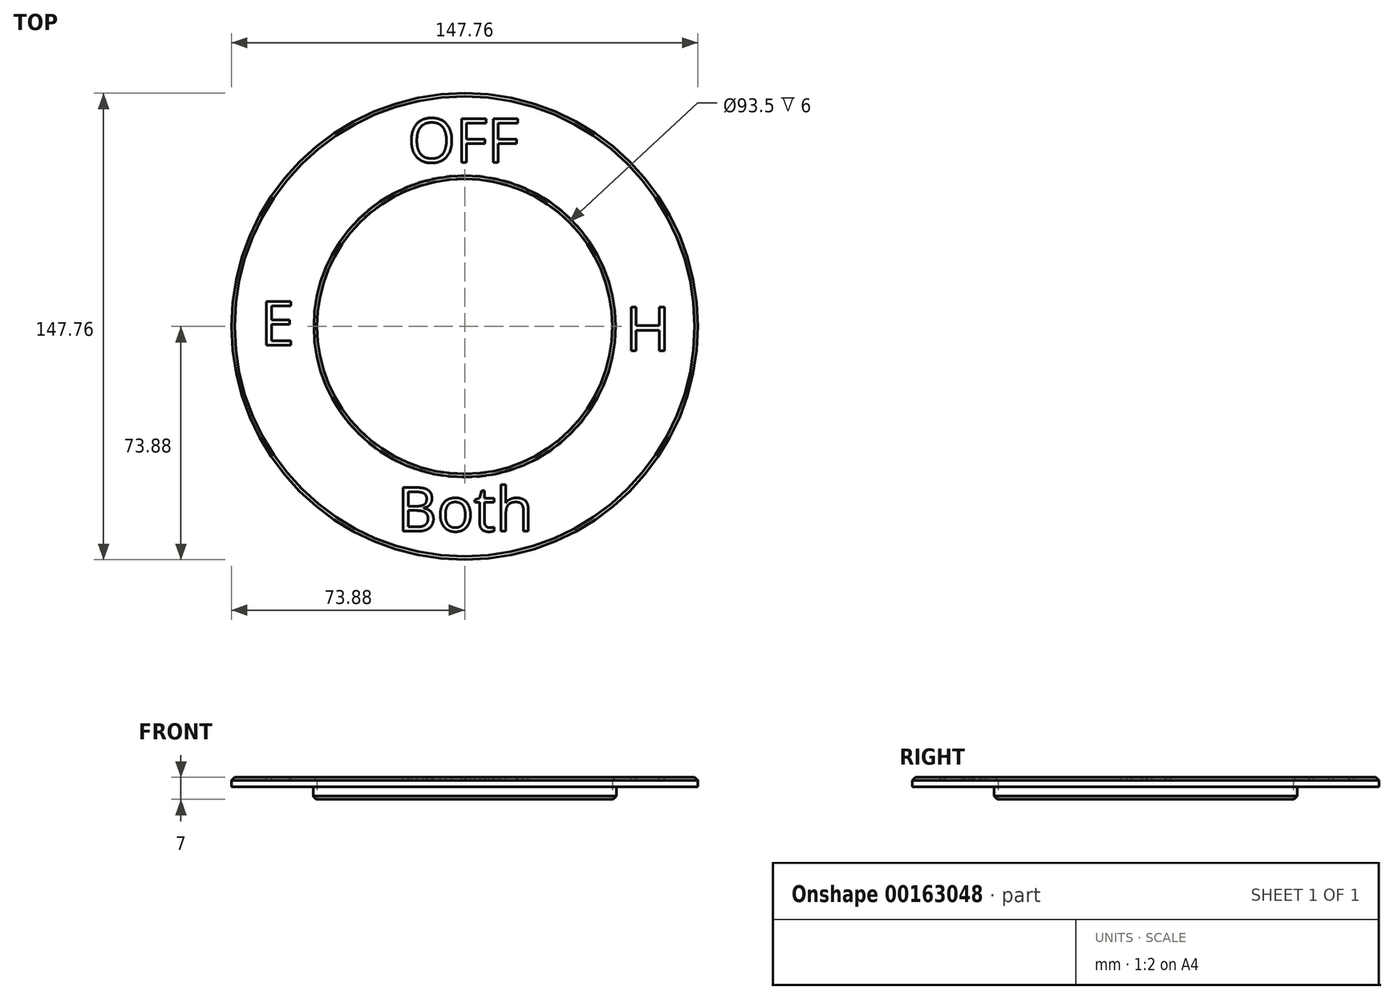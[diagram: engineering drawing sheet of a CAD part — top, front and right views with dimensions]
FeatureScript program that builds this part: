
annotation { "Feature Type Name" : "Feature", "Feature Type Description" : "" }
export const myFeature = defineFeature(function(context is Context, id is Id, definition is map)
    precondition{}
    {
        {
            var Q0;
            Q0=qCreatedBy(makeId("Top.planeOp"),FACE);
            var sketch = newSketch(context, id + "F0", { "sketchPlane" : qUnion([Q0])});
            skCircle(sketch, "E0", {"center": v(0, 0) * mm, "radius": 46.75 * mm});
            skCircle(sketch, "E1", {"center": v(0, 0) * mm, "radius": 53.88 * mm, "construction": true});
            skLineSegment(sketch, "E2", {"start": v(0, 0) * mm, "end": v(95.69, 0) * mm, "construction": true});
            skPoint(sketch, "E3.orphan", {"position": v(-65, -65) * mm});
            skCircle(sketch, "E4.converted", {"center": v(0, 0) * mm, "radius": 73.88 * mm});
            skSolve(sketch);
        }
        {
            var Q0;
            Q0 = qSketchRegion(id + "F0", true);
            extrude(context, id + "F1", {"entities" : qUnion([Q0]), "depth" : 3 * mm});
        }
        {
            var Q0;
            Q0=makeQuery(id+"F1.opExtrude","CAP_FACE",FACE,{"disambiguationData":[OSD([sQuery(id+"F0.wireOp",EDGE,"E0"),sQuery(id+"F0.wireOp",EDGE,"E4.converted")])],"isStart":true});
            var sketch = newSketch(context, id + "F2", { "sketchPlane" : qUnion([Q0])});
            skCircle(sketch, "E5.0", {"center": v(0, 0) * mm, "radius": 46.75 * mm});
            skCircle(sketch, "E6", {"center": v(0, 0) * mm, "radius": 48 * mm});
            skSolve(sketch);
        }
        {
            var Q0;
            Q0 = qSketchRegion(id + "F2", true);
            extrude(context, id + "F3", {"entities" : qUnion([Q0]), "operationType" : NewBodyOperationType.ADD, "depth" : 4 * mm});
        }
        {
            var Q0;
            Q0=makeQuery(id+"F1.opExtrude","CAP_FACE",FACE,{"disambiguationData":[OSD([sQuery(id+"F0.wireOp",EDGE,"E0"),sQuery(id+"F0.wireOp",EDGE,"E4.converted")])],"isStart":false});
            var sketch = newSketch(context, id + "F4", { "sketchPlane" : qUnion([Q0])});
            skText(sketch, "E7", { "text": "OFF", "fontName": "OpenSans-Regular.ttf"});
            skText(sketch, "E8", { "text": "Both", "fontName": "OpenSans-Regular.ttf"});
            skText(sketch, "E9", { "text": "E", "fontName": "OpenSans-Regular.ttf"});
            skLineSegment(sketch, "E10", {"start": v(0, 0) * mm, "end": v(0, 41.18) * mm, "construction": true});
            skText(sketch, "E11", { "text": "H", "fontName": "OpenSans-Regular.ttf"});
            const initialGuessF4  = {"E7": [-0.01804, 0.05198, 1, 0, 0.014], "E8": [-0.02142, -0.0649, 1, 0, 0.014], "E9": [-0.06472, -0.00594, 1, 0, 0.014], "E11": [0.0508, -0.00772, 1, 0, 0.014]};
            skSetInitialGuess(sketch, initialGuessF4);
            skSolve(sketch);
        }
        {
            var Q0;
            Q0 = qSketchRegion(id + "F4", true);
            extrude(context, id + "F5", {"entities" : qUnion([Q0]), "operationType" : NewBodyOperationType.REMOVE, "oppositeDirection" : true, "depth" : 1 * mm});
        }
        {
            var Q0;
            Q0=makeQuery(id+"F1.opExtrude","CAP_EDGE",EDGE,{"disambiguationData":[OSD([sQuery(id+"F0.wireOp",EDGE,"E4.converted")])],"isStart":false});
            var Q1;
            Q1=makeQuery(id+"F1.opExtrude","CAP_EDGE",EDGE,{"disambiguationData":[OSD([sQuery(id+"F0.wireOp",EDGE,"E0")])],"isStart":false});
            var Q2;
            Q2=makeQuery(id+"F3.opExtrude","CAP_EDGE",EDGE,{"disambiguationData":[OSD([sQuery(id+"F2.wireOp",EDGE,"E6")])],"isStart":false});
            chamfer(context, id + "F6", {"entities" : qUnion([Q0, Q1, Q2]), "width" : 1 * mm, "tangentPropagation" : true});
        }
    });
